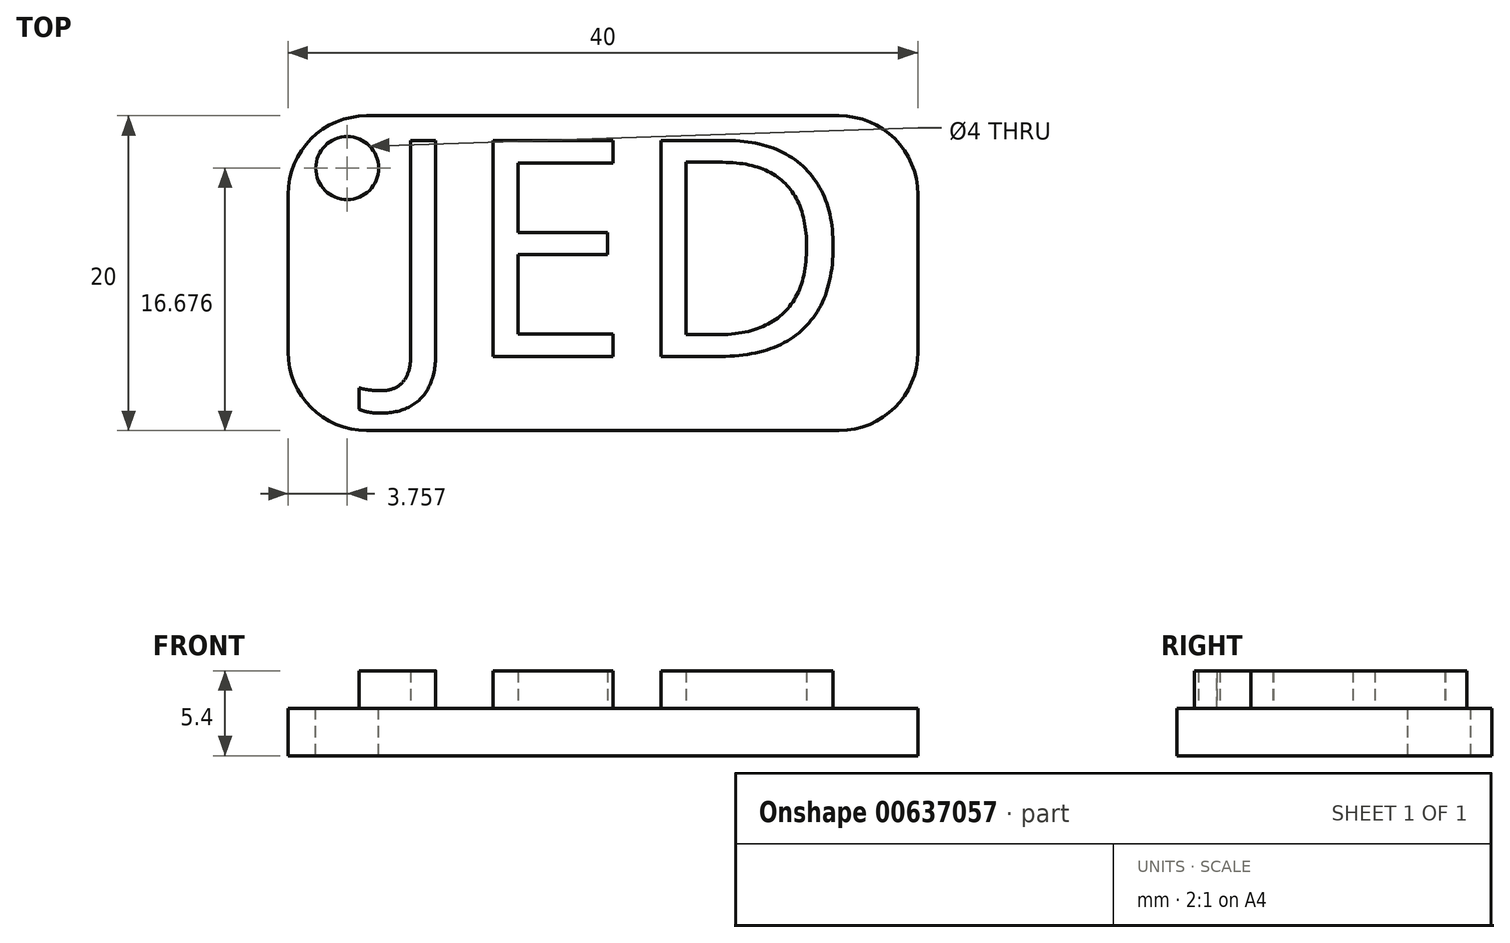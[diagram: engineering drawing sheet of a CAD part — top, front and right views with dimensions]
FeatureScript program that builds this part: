
annotation { "Feature Type Name" : "Feature", "Feature Type Description" : "" }
export const myFeature = defineFeature(function(context is Context, id is Id, definition is map)
    precondition{}
    {
        {
            var Q0;
            Q0=qCreatedBy(makeId("Top.planeOp"),FACE);
            var sketch = newSketch(context, id + "F0", { "sketchPlane" : qUnion([Q0])});
            skLineSegment(sketch, "E0.bottom", {"start": v(0, 0) * mm, "end": v(40, 0) * mm});
            skLineSegment(sketch, "E0.top", {"start": v(0, 20) * mm, "end": v(40, 20) * mm});
            skLineSegment(sketch, "E0.left", {"start": v(0, 0) * mm, "end": v(0, 20) * mm});
            skLineSegment(sketch, "E0.right", {"start": v(40, 0) * mm, "end": v(40, 20) * mm});
            skSolve(sketch);
        }
        {
            var Q0;
            Q0 = qSketchRegion(id + "F0", true);
            extrude(context, id + "F1", {"entities" : qUnion([Q0]), "depth" : 3 * mm, "offsetDistance" : 25 * mm});
        }
        {
            var Q0;
            Q0=makeQuery(id+"F1.opExtrude","CAP_FACE",FACE,{"disambiguationData":[OSD([sQuery(id+"F0.wireOp",EDGE,"E0.bottom"),sQuery(id+"F0.wireOp",EDGE,"E0.top"),sQuery(id+"F0.wireOp",EDGE,"E0.left"),sQuery(id+"F0.wireOp",EDGE,"E0.right")])],"isStart":false});
            var sketch = newSketch(context, id + "F2", { "sketchPlane" : qUnion([Q0])});
            skText(sketch, "E1", { "text": "JED", "fontName": "OpenSans-Regular.ttf"});
            const initialGuessF2  = {"E1": [0.006, 0.00472, 1, 0, 0.01382]};
            skSetInitialGuess(sketch, initialGuessF2);
            skSolve(sketch);
        }
        {
            var Q0;
            Q0 = qSketchRegion(id + "F2", true);
            extrude(context, id + "F3", {"entities" : qUnion([Q0]), "operationType" : NewBodyOperationType.ADD, "depth" : 2.4 * mm, "offsetDistance" : 25 * mm});
        }
        {
            var Q0;
            Q0=makeQuery(id+"F1.opExtrude","SWEPT_EDGE",EDGE,{"disambiguationData":[OSD([sQuery(id+"F0.wireOp",EDGE,"E0.bottom"),sQuery(id+"F0.wireOp",EDGE,"E0.right")])]});
            var Q1;
            Q1=makeQuery(id+"F1.opExtrude","SWEPT_EDGE",EDGE,{"disambiguationData":[OSD([sQuery(id+"F0.wireOp",EDGE,"E0.top"),sQuery(id+"F0.wireOp",EDGE,"E0.right")])]});
            var Q2;
            Q2=makeQuery(id+"F1.opExtrude","SWEPT_EDGE",EDGE,{"disambiguationData":[OSD([sQuery(id+"F0.wireOp",EDGE,"E0.top"),sQuery(id+"F0.wireOp",EDGE,"E0.left")])]});
            var Q3;
            Q3=makeQuery(id+"F1.opExtrude","SWEPT_EDGE",EDGE,{"disambiguationData":[OSD([sQuery(id+"F0.wireOp",EDGE,"E0.bottom"),sQuery(id+"F0.wireOp",EDGE,"E0.left")])]});
            fillet(context, id + "F4", {"entities" : qUnion([Q0, Q1, Q2, Q3]), "radius" : 5 * mm, "tangentPropagation" : true, "allowEdgeOverflow" : false});
        }
        {
            var Q0;
            {var subQ0=sQuery(id+"F0.wireOp",EDGE,"E0.top");var subQ1=sQuery(id+"F0.wireOp",EDGE,"E0.right");var subQ2=sQuery(id+"F0.wireOp",EDGE,"E0.bottom");var subQ3=sQuery(id+"F0.wireOp",EDGE,"E0.left");Q0=makeQuery(id+"F3.boolean.opBoolean","SPLIT",FACE,{"disambiguationData":[TD([makeQuery(id+"F1.opExtrude","SWEPT_FACE",FACE,{"disambiguationData":[OSD([subQ2])]})])],"derivedFrom":makeQuery(id+"F1.opExtrude","CAP_FACE",FACE,{"disambiguationData":[OSD([subQ2,subQ0,subQ3,subQ1])],"isStart":false})});}
            var sketch = newSketch(context, id + "F5", { "sketchPlane" : qUnion([Q0])});
            skPoint(sketch, "E2", {"position": v(3.76, 16.68) * mm});
            skSolve(sketch);
        }
        {
            var Q0;
            Q0=sQuery(id+"F5.wireOp",VERTEX,"E2");
            var Q1;
            Q1=makeQuery(id+"F1.opExtrude","SWEPT_BODY",BODY,{"disambiguationData":[OSD([sQuery(id+"F0.wireOp",EDGE,"E0.bottom"),sQuery(id+"F0.wireOp",EDGE,"E0.top"),sQuery(id+"F0.wireOp",EDGE,"E0.left"),sQuery(id+"F0.wireOp",EDGE,"E0.right")])]});
            hole(context, id + "F6", {"style" : HoleStyle.SIMPLE, "endStyle" : HoleEndStyle.THROUGH, "holeDiameter" : 4 * mm, "majorDiameter" : 5 * mm, "isTappedThrough" : true, "tappedDepth" : 12 * mm, "tapClearance" : 3, "locations" : qUnion([Q0]), "scope" : qUnion([Q1])});
        }
    });
